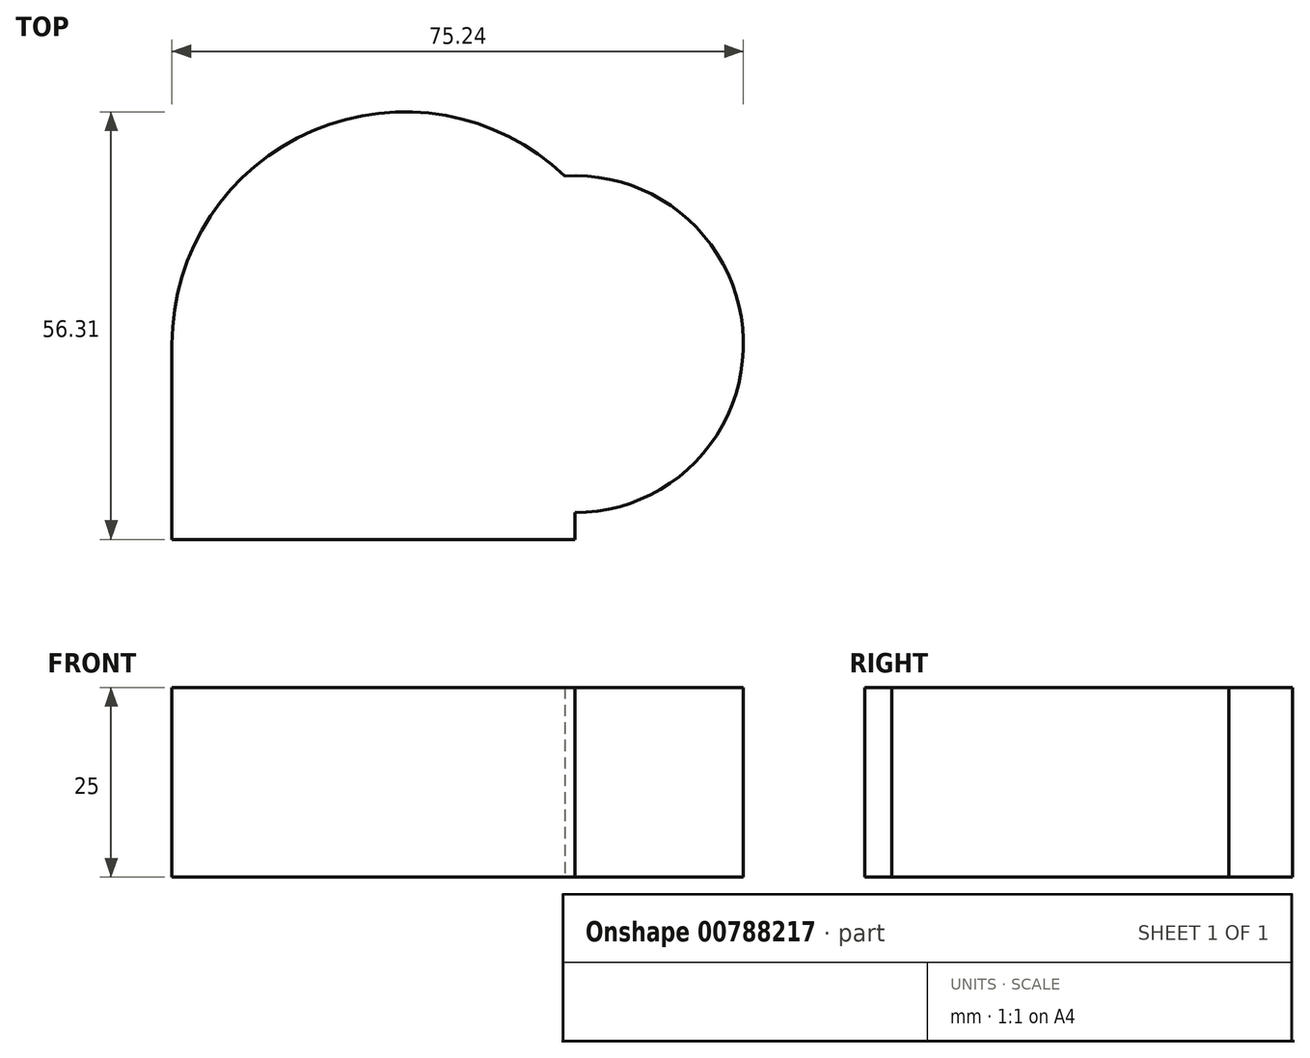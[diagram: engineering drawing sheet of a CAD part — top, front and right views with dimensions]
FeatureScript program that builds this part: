
annotation { "Feature Type Name" : "Feature", "Feature Type Description" : "" }
export const myFeature = defineFeature(function(context is Context, id is Id, definition is map)
    precondition{}
    {
        {
            var Q0;
            Q0=qCreatedBy(makeId("Top.planeOp"),FACE);
            var sketch = newSketch(context, id + "F0", { "sketchPlane" : qUnion([Q0])});
            skLineSegment(sketch, "E0", {"start": v(-43.53, 11.12) * mm, "end": v(-14.33, 72.73) * mm});
            skLineSegment(sketch, "E1.bottom", {"start": v(9.5, 36.83) * mm, "end": v(-43.53, 36.83) * mm});
            skLineSegment(sketch, "E1.top", {"start": v(9.5, 11.12) * mm, "end": v(-43.53, 11.12) * mm});
            skLineSegment(sketch, "E1.left", {"start": v(9.5, 36.83) * mm, "end": v(9.5, 11.12) * mm});
            skLineSegment(sketch, "E1.right", {"start": v(-43.53, 36.83) * mm, "end": v(-43.53, 11.12) * mm});
            skCircle(sketch, "E2", {"center": v(9.5, 36.83) * mm, "radius": 22.2 * mm});
            skArc(sketch, "E3", {"start": v(8.17, 58.99) * mm, "mid": v(-24.98, 64.95) * mm, "end": v(-43.53, 36.83) * mm});
            skSolve(sketch);
        }
        {
            var Q0;
            {var subQ0=sQuery(id+"F0.wireOp",EDGE,"E1.right");Q0=makeQuery(id+"F0.imprint","IMPRINT",FACE,{"disambiguationData":[TD([[makeQuery(id+"F0.imprint","IMPRINT",EDGE,{"derivedFrom":subQ0}),1.0]])]});}
            var Q1;
            {var subQ0=sQuery(id+"F0.wireOp",EDGE,"E3");var subQ1=sQuery(id+"F0.wireOp",EDGE,"E0");var subQ2=makeQuery(id+"F0.imprint","INTERSECT",VERTEX,{"derivedFrom":[subQ1,subQ0]});Q1=makeQuery(id+"F0.imprint","IMPRINT",FACE,{"disambiguationData":[TD([[makeQuery(id+"F0.imprint","IMPRINT",EDGE,{"disambiguationData":[TD([[subQ2,1.0]])],"derivedFrom":subQ1}),1.0]])]});}
            var Q2;
            {var subQ0=sQuery(id+"F0.wireOp",EDGE,"E1.left");var subQ1=sQuery(id+"F0.wireOp",EDGE,"E1.bottom");var subQ2=makeQuery(id+"F0.imprint","INTERSECT",VERTEX,{"derivedFrom":[subQ1,subQ0]});Q2=makeQuery(id+"F0.imprint","IMPRINT",FACE,{"disambiguationData":[TD([[makeQuery(id+"F0.imprint","IMPRINT",EDGE,{"disambiguationData":[TD([[subQ2,-1.0]])],"derivedFrom":subQ1}),-1.0]])]});}
            var Q3;
            {var subQ0=sQuery(id+"F0.wireOp",EDGE,"E1.left");var subQ1=sQuery(id+"F0.wireOp",EDGE,"E1.bottom");var subQ2=makeQuery(id+"F0.imprint","INTERSECT",VERTEX,{"derivedFrom":[subQ1,subQ0]});Q3=makeQuery(id+"F0.imprint","IMPRINT",FACE,{"disambiguationData":[TD([[makeQuery(id+"F0.imprint","IMPRINT",EDGE,{"disambiguationData":[TD([[subQ2,-1.0]])],"derivedFrom":subQ1}),1.0]])]});}
            var Q4;
            {var subQ1=sQuery(id+"F0.wireOp",EDGE,"E1.top");Q4=makeQuery(id+"F0.imprint","IMPRINT",FACE,{"disambiguationData":[TD([[makeQuery(id+"F0.imprint","IMPRINT",EDGE,{"derivedFrom":subQ1}),-1.0]])]});}
            var Q5;
            {var subQ0=sQuery(id+"F0.wireOp",EDGE,"E3");var subQ1=sQuery(id+"F0.wireOp",EDGE,"E0");var subQ2=makeQuery(id+"F0.imprint","INTERSECT",VERTEX,{"derivedFrom":[subQ1,subQ0]});Q5=makeQuery(id+"F0.imprint","IMPRINT",FACE,{"disambiguationData":[TD([[makeQuery(id+"F0.imprint","IMPRINT",EDGE,{"disambiguationData":[TD([[subQ2,1.0]])],"derivedFrom":subQ1}),-1.0]])]});}
            extrude(context, id + "F1", {"entities" : qUnion([Q0, Q1, Q2, Q3, Q4, Q5]), "depth" : 25 * mm, "offsetDistance" : 25 * mm});
        }
    });
